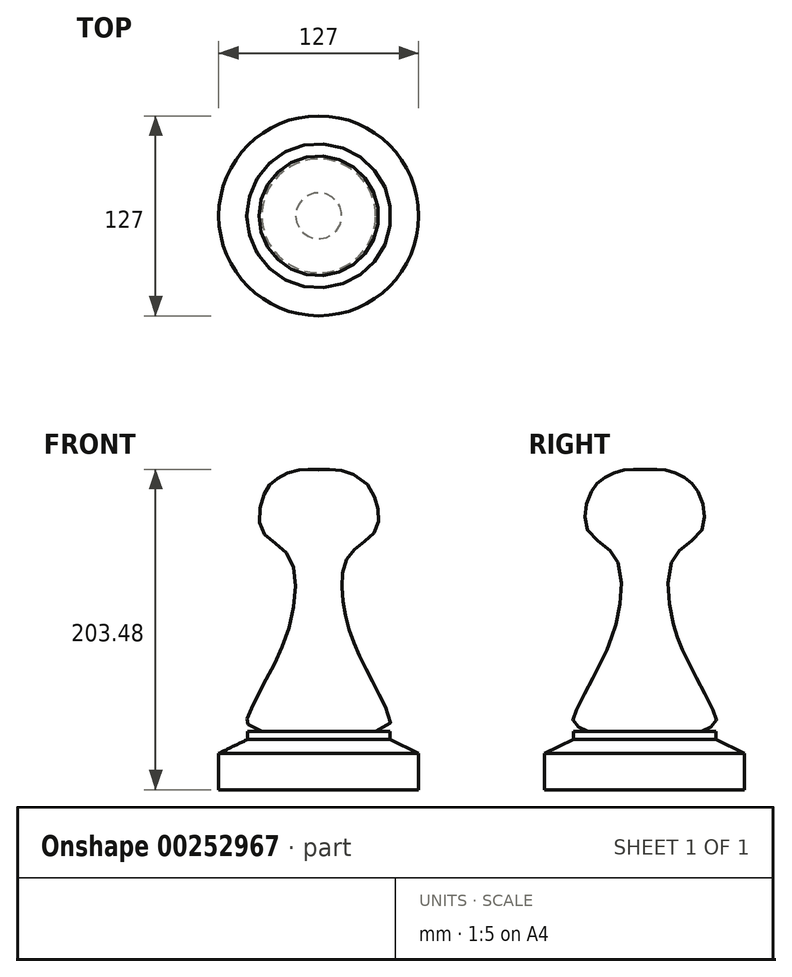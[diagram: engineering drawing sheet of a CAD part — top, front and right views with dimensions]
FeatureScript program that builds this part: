
annotation { "Feature Type Name" : "Feature", "Feature Type Description" : "" }
export const myFeature = defineFeature(function(context is Context, id is Id, definition is map)
    precondition{}
    {
        {
            var Q0;
            Q0=qCreatedBy(makeId("Front.planeOp"),FACE);
            var sketch = newSketch(context, id + "F0", { "sketchPlane" : qUnion([Q0])});
            skLineSegment(sketch, "E0", {"start": v(0, 99.55) * mm, "end": v(0, -103.65) * mm, "construction": true});
            skLineSegment(sketch, "E1", {"start": v(0, -103.65) * mm, "end": v(-63.5, -103.65) * mm});
            skLineSegment(sketch, "E2", {"start": v(-63.5, -103.65) * mm, "end": v(-63.5, -80.56) * mm});
            skLineSegment(sketch, "E3", {"start": v(-63.5, -80.56) * mm, "end": v(-45.2, -71.72) * mm});
            skLineSegment(sketch, "E4", {"start": v(-45.2, -71.72) * mm, "end": v(-45.2, -66.72) * mm});
            skLineSegment(sketch, "E5", {"start": v(-45.2, -66.72) * mm, "end": v(-36.09, -66.72) * mm});
            skFitSpline(sketch, "E6", {"points": [v(-36.09, -66.72) * mm, v(-45.57, -59.07) * mm, v(-36.09, -38.66) * mm, v(-18.96, -0.75) * mm, v(-18.6, 44.1) * mm, v(-36.09, 60.86) * mm, v(-35, 83.46) * mm, v(-26.25, 94.04) * mm, v(-11.66, 99.55) * mm, v(0, 99.55) * mm], "startDerivative": vector(-343.27, 158.05) * mm, "endDerivative": vector(108.93, -3.69) * mm});
            skSolve(sketch);
        }
        {
            var Q0;
            Q0 = qSketchRegion(id + "F0", true);
            var Q1;
            Q1=sQuery(id+"F0.wireOp",EDGE,"E6");
            var Q2;
            Q2=sQuery(id+"F0.wireOp",EDGE,"E5");
            var Q3;
            Q3=sQuery(id+"F0.wireOp",EDGE,"E4");
            var Q4;
            Q4=sQuery(id+"F0.wireOp",EDGE,"E3");
            var Q5;
            Q5=sQuery(id+"F0.wireOp",EDGE,"E2");
            var Q6;
            Q6=sQuery(id+"F0.wireOp",EDGE,"E1");
            var Q7;
            Q7=sQuery(id+"F0.wireOp",EDGE,"E0");
            revolve(context, id + "F1", {"bodyType" : ToolBodyType.SURFACE, "entities" : qUnion([Q0]), "surfaceEntities" : qUnion([Q1, Q2, Q3, Q4, Q5, Q6]), "axis" : qUnion([Q7]), "revolveType" : RevolveType.FULL});
        }
    });
